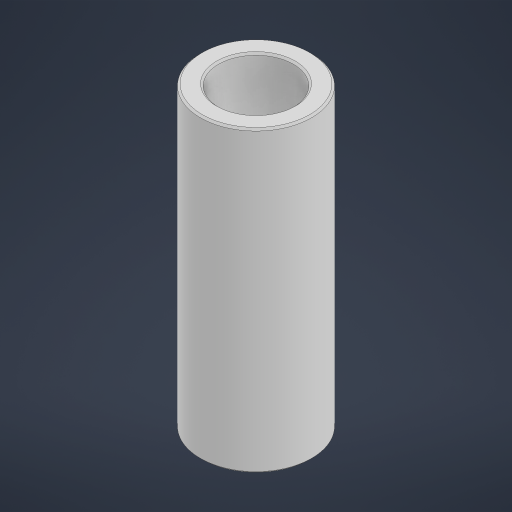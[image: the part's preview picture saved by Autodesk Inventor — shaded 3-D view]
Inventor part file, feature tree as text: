
AUTODESK INVENTOR PART (.ipt)
format: ipt  version: 2023 (Build 270158000, 158)  size: 176,640 bytes
history: native  units: in
note: dims shown in document units (in); Inventor stores cm internally (conversion verified against a paired STEP export)
features: chamfer x1
ambient origin geometry x8: Origin, YZ Plane, XZ Plane, XY Plane, X Axis, Y Axis, Z Axis, Center Point
bodies: Solid1 (feature_tree)
feature tree (1):
  chamfer  "Chamfer1"  [1 undecoded]
note: 1 required parameter value undecoded (feature->parameter linkage not recoverable at this tier; creation-order binding heuristic only, values carry confidence <= 0.55)
